# Revit family: Control_Unit-Lutron-QSPS-DH-1-75-H
name_source: partatom
category: Lighting Devices
revit_build: Autodesk Revit 2017 (Build: 20160225_1515(x64)
units: mm (PartAtom-declared; Revit-internal decimal feet)

## family parameters
Cut with Voids When Loaded = No
Host = Face
Maintain Annotation Orientation = Yes
OmniClass Number = 23.85.80.11
OmniClass Title = Building Controls
Part Type = Normal
Room Calculation Point = No
Round Connector Dimension = Use Radius
Shared = No

## types (1)
- QSPS-DH-1-75-H
    Apparent Power = 130 VA
    Assembly Code = D5020200
    Cost = 0 $
    Current = 1 A
    Default Elevation = 4' - 0"
    Description = The HomeWorks® QS Power Supply provides power to the HomeWorks® QS processor as well as system devices and interfaces.
    Finish = Plastic - Lutron - White - Matte
    Instruction Sheet Link = http://www.lutron.com
    Load Classification = Other
    Manufacturer = Lutron Electronics Co., Inc
    Manufacturer Fax Number = 610-282-1243
    Maximum Operating Temperature = 131 °F
    Minimum Operating Temperature = 32 °F
    Model = QSPS-DH-1-75-H
    Number of Poles = 1
    Operating Voltage = 100 V~ to 277 V~ 50/60 Hz
    Overall Depth = 0' - 2 13/32"
    Overall Height = 0' - 3 17/32"
    Overall Width = 0' - 3 17/32"
    Performance URL = http://www.lutron.com
    Product Documentation Link = http://www.lutron.com
    Product Name = QSPS-DH-1-75-H Power Supply with Wire Harness
    Product Page URL = http://www.lutron.com
    Series = HomeWorks
    URL = http://www.lutron.com
    Version = 2017 - v1.0a
    Video Link = https://www.youtube.com
    Voltage = 100 V
    Warranty URL = http://www.lutron.com

## geometry (parser evidence)
native form markers: Sweep x2
no freeform markers — native parametric forms only
